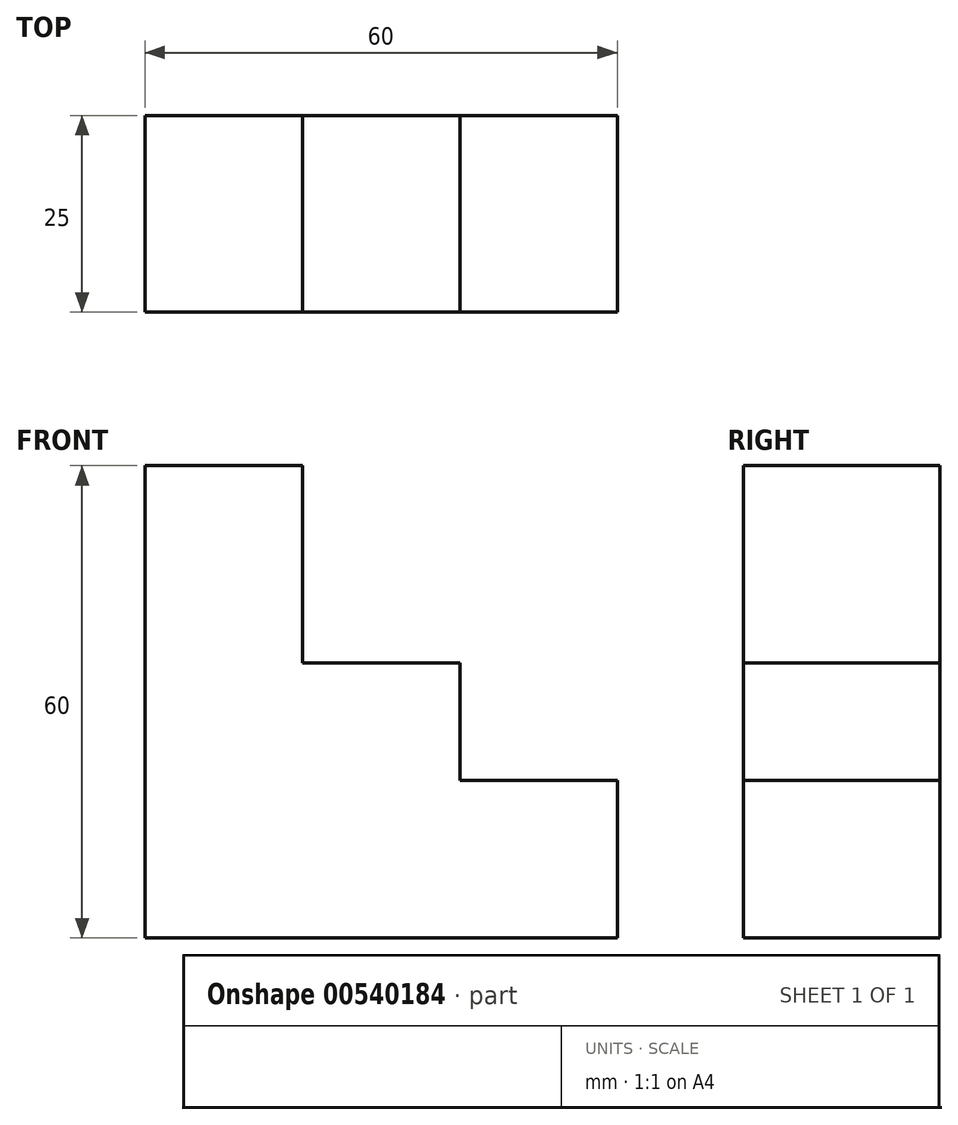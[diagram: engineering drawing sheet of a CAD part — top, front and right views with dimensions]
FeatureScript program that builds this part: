
annotation { "Feature Type Name" : "Feature", "Feature Type Description" : "" }
export const myFeature = defineFeature(function(context is Context, id is Id, definition is map)
    precondition{}
    {
        {
            var Q0;
            Q0=qCreatedBy(makeId("Front.planeOp"),FACE);
            var sketch = newSketch(context, id + "F0", { "sketchPlane" : qUnion([Q0])});
            skLineSegment(sketch, "E0", {"start": v(-64.96, 40) * mm, "end": v(-44.96, 40) * mm});
            skLineSegment(sketch, "E1", {"start": v(-44.96, 40) * mm, "end": v(-44.96, 14.93) * mm});
            skLineSegment(sketch, "E2", {"start": v(-44.96, 14.93) * mm, "end": v(-24.96, 14.93) * mm});
            skLineSegment(sketch, "E3", {"start": v(-24.96, 14.93) * mm, "end": v(-24.96, 0) * mm});
            skLineSegment(sketch, "E4", {"start": v(-24.96, 0) * mm, "end": v(-4.96, 0) * mm});
            skLineSegment(sketch, "E5", {"start": v(-4.96, 0) * mm, "end": v(-4.96, -20) * mm});
            skLineSegment(sketch, "E6", {"start": v(-4.96, -20) * mm, "end": v(-64.96, -20) * mm});
            skLineSegment(sketch, "E7", {"start": v(-64.96, 40) * mm, "end": v(-64.96, -20) * mm});
            skSolve(sketch);
        }
        {
            var Q0;
            Q0 = qSketchRegion(id + "F0", true);
            extrude(context, id + "F1", {"entities" : qUnion([Q0]), "depth" : 25 * mm, "offsetDistance" : 25 * mm});
        }
    });
